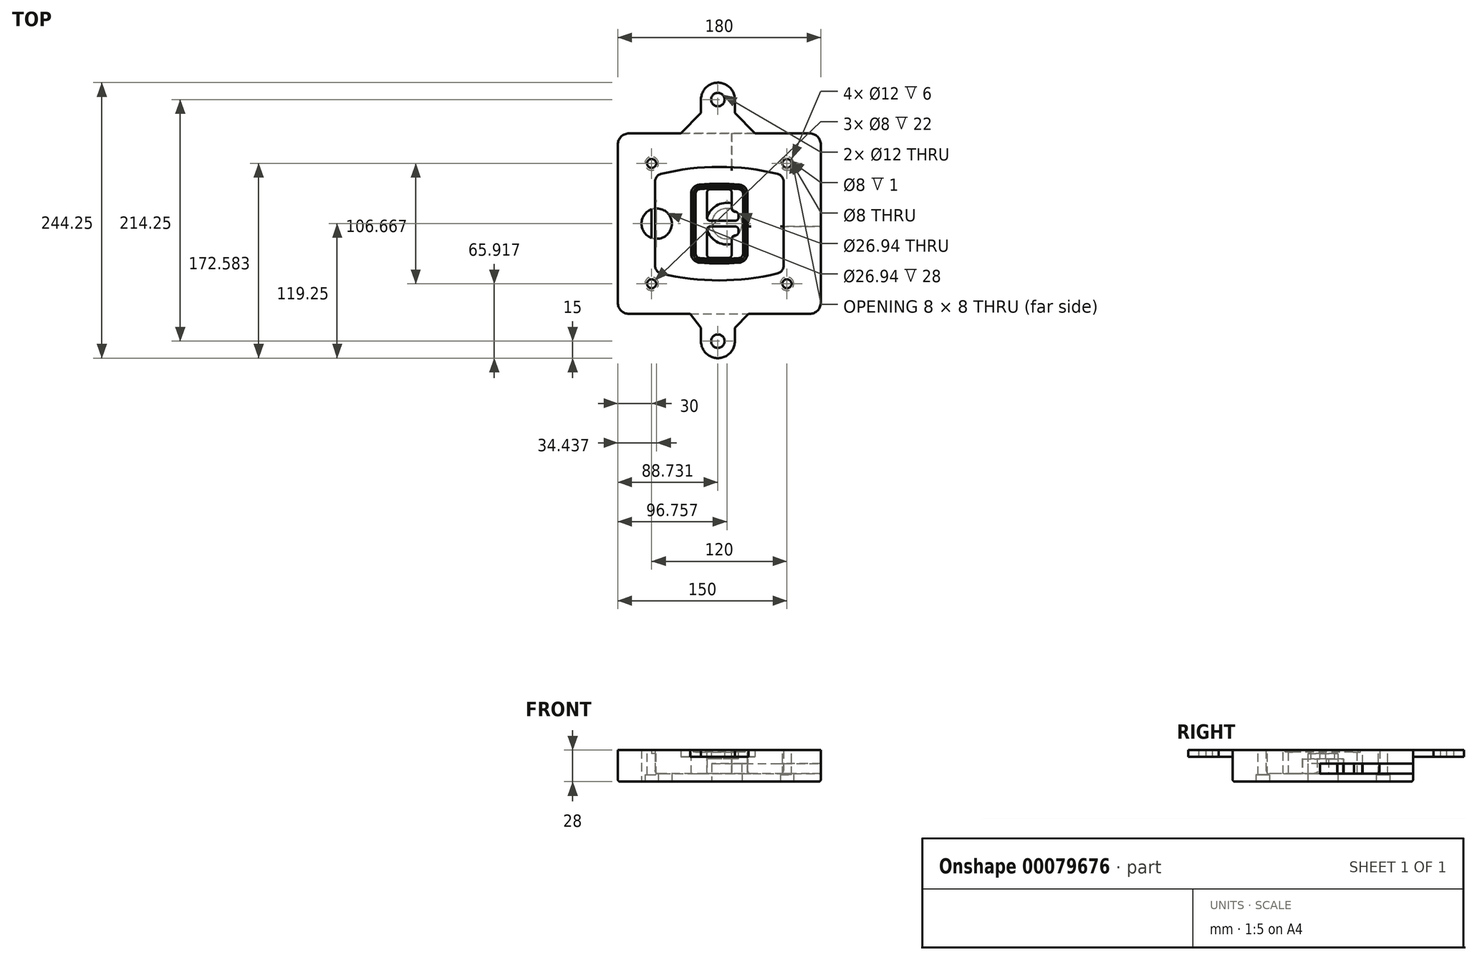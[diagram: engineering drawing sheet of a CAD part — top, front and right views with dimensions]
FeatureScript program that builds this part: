
annotation { "Feature Type Name" : "Feature", "Feature Type Description" : "" }
export const myFeature = defineFeature(function(context is Context, id is Id, definition is map)
    precondition{}
    {
        {
            var Q0;
            Q0=qCreatedBy(makeId("Top.planeOp"),FACE);
            var sketch = newSketch(context, id + "F0", { "sketchPlane" : qUnion([Q0])});
            skPoint(sketch, "E0.rect.middle", {"position": v(0, 0) * mm});
            skLineSegment(sketch, "E1.bottom", {"start": v(-80, -80) * mm, "end": v(80, -80) * mm});
            skLineSegment(sketch, "E1.top", {"start": v(-80, 80) * mm, "end": v(80, 80) * mm});
            skLineSegment(sketch, "E1.left", {"start": v(-90, -70) * mm, "end": v(-90, 70) * mm});
            skLineSegment(sketch, "E1.right", {"start": v(90, -70) * mm, "end": v(90, 70) * mm});
            skLineSegment(sketch, "E2", {"start": v(-90, 80) * mm, "end": v(90, -80) * mm, "construction": true});
            skLineSegment(sketch, "E3", {"start": v(90, 80) * mm, "end": v(-90, -80) * mm, "construction": true});
            skCircle(sketch, "E4", {"center": v(-60, 53.33) * mm, "radius": 4 * mm});
            skCircle(sketch, "E5", {"center": v(60, 53.33) * mm, "radius": 4 * mm});
            skCircle(sketch, "E6", {"center": v(60, -53.33) * mm, "radius": 4 * mm});
            skCircle(sketch, "E7", {"center": v(-60, -53.33) * mm, "radius": 4 * mm});
            skLineSegment(sketch, "E8", {"start": v(-60, 53.33) * mm, "end": v(60, 53.33) * mm, "construction": true});
            skLineSegment(sketch, "E9", {"start": v(60, 53.33) * mm, "end": v(60, -53.33) * mm, "construction": true});
            skLineSegment(sketch, "E10", {"start": v(60, -53.33) * mm, "end": v(-60, -53.33) * mm, "construction": true});
            skLineSegment(sketch, "E11", {"start": v(-60, -53.33) * mm, "end": v(-60, 53.33) * mm, "construction": true});
            skLineSegment(sketch, "E12", {"start": v(-60, 37.3) * mm, "end": v(-60, -37.3) * mm});
            skLineSegment(sketch, "E13", {"start": v(60, 37.3) * mm, "end": v(60, -37.3) * mm});
            skArc(sketch, "E14", {"start": v(52.38, 47.01) * mm, "mid": v(0, 53.33) * mm, "end": v(-52.38, 47.01) * mm});
            skArc(sketch, "E15", {"start": v(-52.38, -47.01) * mm, "mid": v(0, -53.33) * mm, "end": v(52.38, -47.01) * mm});
            skLineSegment(sketch, "E16", {"start": v(-60, 0) * mm, "end": v(60, 0) * mm, "construction": true});
            skPoint(sketch, "E17.visualSharp", {"position": v(-60, -45) * mm});
            skArc(sketch, "E17.filletArc", {"start": v(-60, -37.3) * mm, "mid": v(-57.87, -43.47) * mm, "end": v(-52.38, -47.01) * mm});
            skPoint(sketch, "E18.visualSharp", {"position": v(-60, 45) * mm});
            skArc(sketch, "E18.filletArc", {"start": v(-52.38, 47.01) * mm, "mid": v(-57.87, 43.47) * mm, "end": v(-60, 37.3) * mm});
            skPoint(sketch, "E19.visualSharp", {"position": v(60, 45) * mm});
            skArc(sketch, "E19.filletArc", {"start": v(60, 37.3) * mm, "mid": v(57.87, 43.47) * mm, "end": v(52.38, 47.01) * mm});
            skPoint(sketch, "E20.visualSharp", {"position": v(60, -45) * mm});
            skArc(sketch, "E20.filletArc", {"start": v(52.38, -47.01) * mm, "mid": v(57.87, -43.47) * mm, "end": v(60, -37.3) * mm});
            skPoint(sketch, "E21.visualSharp", {"position": v(-90, 80) * mm});
            skArc(sketch, "E21.filletArc", {"start": v(-80, 80) * mm, "mid": v(-87.07, 77.07) * mm, "end": v(-90, 70) * mm});
            skPoint(sketch, "E22.visualSharp", {"position": v(90, 80) * mm});
            skArc(sketch, "E22.filletArc", {"start": v(90, 70) * mm, "mid": v(87.07, 77.07) * mm, "end": v(80, 80) * mm});
            skPoint(sketch, "E23.visualSharp", {"position": v(90, -80) * mm});
            skArc(sketch, "E23.filletArc", {"start": v(80, -80) * mm, "mid": v(87.07, -77.07) * mm, "end": v(90, -70) * mm});
            skPoint(sketch, "E24.visualSharp", {"position": v(-90, -80) * mm});
            skArc(sketch, "E24.filletArc", {"start": v(-90, -70) * mm, "mid": v(-87.07, -77.07) * mm, "end": v(-80, -80) * mm});
            skArc(sketch, "E25.0", {"start": v(57, 37.3) * mm, "mid": v(55.5, 41.62) * mm, "end": v(51.67, 44.1) * mm});
            skLineSegment(sketch, "E25.1", {"start": v(57, 37.3) * mm, "end": v(57, -37.3) * mm});
            skArc(sketch, "E25.2", {"start": v(51.67, -44.1) * mm, "mid": v(55.5, -41.62) * mm, "end": v(57, -37.3) * mm});
            skArc(sketch, "E25.3", {"start": v(-51.67, -44.1) * mm, "mid": v(0, -50.33) * mm, "end": v(51.67, -44.1) * mm});
            skArc(sketch, "E25.4", {"start": v(-57, -37.3) * mm, "mid": v(-55.5, -41.62) * mm, "end": v(-51.67, -44.1) * mm});
            skArc(sketch, "E25.5", {"start": v(51.67, 44.1) * mm, "mid": v(0, 50.33) * mm, "end": v(-51.67, 44.1) * mm});
            skLineSegment(sketch, "E25.6", {"start": v(-57, 37.3) * mm, "end": v(-57, -37.3) * mm});
            skArc(sketch, "E25.7", {"start": v(-51.67, 44.1) * mm, "mid": v(-55.5, 41.62) * mm, "end": v(-57, 37.3) * mm});
            skArc(sketch, "E26.0", {"start": v(-53.33, 50.9) * mm, "mid": v(-61.01, 45.94) * mm, "end": v(-64, 37.3) * mm});
            skArc(sketch, "E26.1", {"start": v(53.33, 50.9) * mm, "mid": v(0, 57.33) * mm, "end": v(-53.33, 50.9) * mm});
            skArc(sketch, "E26.2", {"start": v(64, 37.3) * mm, "mid": v(61.01, 45.94) * mm, "end": v(53.33, 50.9) * mm});
            skLineSegment(sketch, "E26.3", {"start": v(64, 37.3) * mm, "end": v(64, -37.3) * mm});
            skArc(sketch, "E26.4", {"start": v(53.33, -50.9) * mm, "mid": v(61.01, -45.94) * mm, "end": v(64, -37.3) * mm});
            skLineSegment(sketch, "E26.5", {"start": v(-64, 37.3) * mm, "end": v(-64, -37.3) * mm});
            skArc(sketch, "E26.6", {"start": v(-53.33, -50.9) * mm, "mid": v(0, -57.33) * mm, "end": v(53.33, -50.9) * mm});
            skArc(sketch, "E26.7", {"start": v(-64, -37.3) * mm, "mid": v(-61.01, -45.94) * mm, "end": v(-53.33, -50.9) * mm});
            skSolve(sketch);
        }
        {
            var Q0;
            Q0=makeQuery(id+"F0.imprint","IMPRINT",FACE,{"disambiguationData":[TD([[makeQuery(id+"F0.imprint","IMPRINT",EDGE,{"derivedFrom":sQuery(id+"F0.wireOp",EDGE,"E1.bottom")}),1.0]])]});
            var Q1;
            Q1=makeQuery(id+"F0.imprint","IMPRINT",FACE,{"disambiguationData":[TD([[makeQuery(id+"F0.imprint","IMPRINT",EDGE,{"derivedFrom":sQuery(id+"F0.wireOp",EDGE,"E12")}),1.0]])]});
            var Q2;
            Q2=makeQuery(id+"F0.imprint","IMPRINT",FACE,{"disambiguationData":[TD([[makeQuery(id+"F0.imprint","IMPRINT",EDGE,{"derivedFrom":sQuery(id+"F0.wireOp",EDGE,"E25.0")}),1.0]])]});
            var Q3;
            Q3=makeQuery(id+"F0.imprint","IMPRINT",FACE,{"disambiguationData":[TD([[makeQuery(id+"F0.imprint","IMPRINT",EDGE,{"derivedFrom":sQuery(id+"F0.wireOp",EDGE,"E12")}),-1.0]])]});
            extrude(context, id + "F1", {"entities" : qUnion([Q0, Q1, Q2, Q3]), "oppositeDirection" : true, "depth" : 25 * mm});
        }
        {
            var Q0;
            Q0=makeQuery(id+"F0.imprint","IMPRINT",FACE,{"disambiguationData":[TD([[makeQuery(id+"F0.imprint","IMPRINT",EDGE,{"derivedFrom":sQuery(id+"F0.wireOp",EDGE,"E12")}),1.0]])]});
            extrude(context, id + "F2", {"entities" : qUnion([Q0]), "operationType" : NewBodyOperationType.ADD, "depth" : 3 * mm});
        }
        {
            var Q0;
            Q0=makeQuery(id+"F0.imprint","IMPRINT",FACE,{"disambiguationData":[TD([[makeQuery(id+"F0.imprint","IMPRINT",EDGE,{"derivedFrom":sQuery(id+"F0.wireOp",EDGE,"E25.0")}),1.0]])]});
            extrude(context, id + "F3", {"entities" : qUnion([Q0]), "operationType" : NewBodyOperationType.REMOVE, "oppositeDirection" : true, "depth" : 18 * mm});
        }
        {
            var Q0;
            Q0=makeQuery(id+"F2.opExtrude","CAP_FACE",FACE,{"disambiguationData":[OSD([sQuery(id+"F0.wireOp",EDGE,"E12"),sQuery(id+"F0.wireOp",EDGE,"E13"),sQuery(id+"F0.wireOp",EDGE,"E14"),sQuery(id+"F0.wireOp",EDGE,"E15"),sQuery(id+"F0.wireOp",EDGE,"E17.filletArc"),sQuery(id+"F0.wireOp",EDGE,"E18.filletArc"),sQuery(id+"F0.wireOp",EDGE,"E19.filletArc"),sQuery(id+"F0.wireOp",EDGE,"E20.filletArc"),sQuery(id+"F0.wireOp",EDGE,"E25.0"),sQuery(id+"F0.wireOp",EDGE,"E25.1"),sQuery(id+"F0.wireOp",EDGE,"E25.2"),sQuery(id+"F0.wireOp",EDGE,"E25.3"),sQuery(id+"F0.wireOp",EDGE,"E25.4"),sQuery(id+"F0.wireOp",EDGE,"E25.5"),sQuery(id+"F0.wireOp",EDGE,"E25.6"),sQuery(id+"F0.wireOp",EDGE,"E25.7")])],"isStart":false});
            var sketch = newSketch(context, id + "F4", { "sketchPlane" : qUnion([Q0])});
            skArc(sketch, "E27.0", {"start": v(-17.7, -34.56) * mm, "mid": v(0, -35.33) * mm, "end": v(17.7, -34.56) * mm});
            skArc(sketch, "E28.0", {"start": v(17.7, 34.56) * mm, "mid": v(0, 35.33) * mm, "end": v(-17.7, 34.56) * mm});
            skLineSegment(sketch, "E29", {"start": v(-25, 26.59) * mm, "end": v(-25, -26.59) * mm});
            skLineSegment(sketch, "E30", {"start": v(25, 26.59) * mm, "end": v(25, -26.59) * mm});
            skLineSegment(sketch, "E31", {"start": v(-25, 33.78) * mm, "end": v(25, 33.78) * mm, "construction": true});
            skLineSegment(sketch, "E32", {"start": v(-25, -33.78) * mm, "end": v(25, -33.78) * mm, "construction": true});
            skPoint(sketch, "E33.visualSharp", {"position": v(-25, 33.78) * mm});
            skArc(sketch, "E33.filletArc", {"start": v(-17.7, 34.56) * mm, "mid": v(-22.9, 32) * mm, "end": v(-25, 26.59) * mm});
            skPoint(sketch, "E34.visualSharp", {"position": v(25, 33.78) * mm});
            skArc(sketch, "E34.filletArc", {"start": v(25, 26.59) * mm, "mid": v(22.9, 32) * mm, "end": v(17.7, 34.56) * mm});
            skPoint(sketch, "E35.visualSharp", {"position": v(25, -33.78) * mm});
            skArc(sketch, "E35.filletArc", {"start": v(17.7, -34.56) * mm, "mid": v(22.9, -32) * mm, "end": v(25, -26.59) * mm});
            skPoint(sketch, "E36.visualSharp", {"position": v(-25, -33.78) * mm});
            skArc(sketch, "E36.filletArc", {"start": v(-25, -26.59) * mm, "mid": v(-22.9, -32) * mm, "end": v(-17.7, -34.56) * mm});
            skArc(sketch, "E37.0", {"start": v(51.67, 44.1) * mm, "mid": v(0, 50.33) * mm, "end": v(-51.67, 44.1) * mm});
            skArc(sketch, "E37.1", {"start": v(-51.67, 44.1) * mm, "mid": v(-55.5, 41.62) * mm, "end": v(-57, 37.3) * mm});
            skLineSegment(sketch, "E37.2", {"start": v(-57, 37.3) * mm, "end": v(-57, -37.3) * mm});
            skArc(sketch, "E37.3", {"start": v(-57, -37.3) * mm, "mid": v(-55.5, -41.62) * mm, "end": v(-51.67, -44.1) * mm});
            skArc(sketch, "E37.4", {"start": v(-51.67, -44.1) * mm, "mid": v(0, -50.33) * mm, "end": v(51.67, -44.1) * mm});
            skArc(sketch, "E37.5", {"start": v(51.67, -44.1) * mm, "mid": v(55.5, -41.62) * mm, "end": v(57, -37.3) * mm});
            skLineSegment(sketch, "E37.6", {"start": v(57, 37.3) * mm, "end": v(57, -37.3) * mm});
            skArc(sketch, "E37.7", {"start": v(57, 37.3) * mm, "mid": v(55.5, 41.62) * mm, "end": v(51.67, 44.1) * mm});
            skLineSegment(sketch, "E38.0", {"start": v(23, 26.59) * mm, "end": v(23, -26.59) * mm});
            skArc(sketch, "E38.1", {"start": v(17.53, -32.56) * mm, "mid": v(21.42, -30.64) * mm, "end": v(23, -26.59) * mm});
            skArc(sketch, "E38.2", {"start": v(-17.53, -32.56) * mm, "mid": v(0, -33.33) * mm, "end": v(17.53, -32.56) * mm});
            skArc(sketch, "E38.3", {"start": v(-23, -26.59) * mm, "mid": v(-21.42, -30.64) * mm, "end": v(-17.53, -32.56) * mm});
            skLineSegment(sketch, "E38.4", {"start": v(-23, 26.59) * mm, "end": v(-23, -26.59) * mm});
            skArc(sketch, "E38.5", {"start": v(23, 26.59) * mm, "mid": v(21.42, 30.64) * mm, "end": v(17.53, 32.56) * mm});
            skArc(sketch, "E38.6", {"start": v(-17.53, 32.56) * mm, "mid": v(-21.42, 30.64) * mm, "end": v(-23, 26.59) * mm});
            skArc(sketch, "E38.7", {"start": v(17.53, 32.56) * mm, "mid": v(0, 33.33) * mm, "end": v(-17.53, 32.56) * mm});
            skArc(sketch, "E39.0", {"start": v(21, 26.59) * mm, "mid": v(19.95, 29.29) * mm, "end": v(17.35, 30.57) * mm});
            skLineSegment(sketch, "E39.1", {"start": v(21, 26.59) * mm, "end": v(21, -26.59) * mm});
            skArc(sketch, "E39.2", {"start": v(17.35, -30.57) * mm, "mid": v(19.95, -29.29) * mm, "end": v(21, -26.59) * mm});
            skArc(sketch, "E39.3", {"start": v(-17.35, -30.57) * mm, "mid": v(0, -31.33) * mm, "end": v(17.35, -30.57) * mm});
            skArc(sketch, "E39.4", {"start": v(-21, -26.59) * mm, "mid": v(-19.95, -29.29) * mm, "end": v(-17.35, -30.57) * mm});
            skArc(sketch, "E39.5", {"start": v(17.35, 30.57) * mm, "mid": v(0, 31.33) * mm, "end": v(-17.35, 30.57) * mm});
            skLineSegment(sketch, "E39.6", {"start": v(-21, 26.59) * mm, "end": v(-21, -26.59) * mm});
            skArc(sketch, "E39.7", {"start": v(-17.35, 30.57) * mm, "mid": v(-19.95, 29.29) * mm, "end": v(-21, 26.59) * mm});
            skLineSegment(sketch, "E40", {"start": v(-25, 0) * mm, "end": v(25, 0) * mm, "construction": true});
            skLineSegment(sketch, "E41", {"start": v(-11, 5.5) * mm, "end": v(-11, 27.5) * mm});
            skLineSegment(sketch, "E42", {"start": v(-8, 30.5) * mm, "end": v(8, 30.5) * mm});
            skLineSegment(sketch, "E43", {"start": v(11, 27.5) * mm, "end": v(11, 13.5) * mm});
            skLineSegment(sketch, "E44", {"start": v(14, 10.5) * mm, "end": v(14, 10.5) * mm});
            skLineSegment(sketch, "E45", {"start": v(17, 7.5) * mm, "end": v(17, 5.5) * mm});
            skLineSegment(sketch, "E46", {"start": v(14, 2.5) * mm, "end": v(-8, 2.5) * mm});
            skPoint(sketch, "E47.visualSharp", {"position": v(-11, 30.5) * mm});
            skArc(sketch, "E47.filletArc", {"start": v(-8, 30.5) * mm, "mid": v(-10.12, 29.62) * mm, "end": v(-11, 27.5) * mm});
            skPoint(sketch, "E48.visualSharp", {"position": v(11, 30.5) * mm});
            skArc(sketch, "E48.filletArc", {"start": v(11, 27.5) * mm, "mid": v(10.12, 29.62) * mm, "end": v(8, 30.5) * mm});
            skPoint(sketch, "E49.visualSharp", {"position": v(11, 10.5) * mm});
            skArc(sketch, "E49.filletArc", {"start": v(11, 13.5) * mm, "mid": v(11.88, 11.38) * mm, "end": v(14, 10.5) * mm});
            skPoint(sketch, "E50.visualSharp", {"position": v(17, 10.5) * mm});
            skArc(sketch, "E50.filletArc", {"start": v(17, 7.5) * mm, "mid": v(16.12, 9.62) * mm, "end": v(14, 10.5) * mm});
            skPoint(sketch, "E51.visualSharp", {"position": v(17, 2.5) * mm});
            skArc(sketch, "E51.filletArc", {"start": v(14, 2.5) * mm, "mid": v(16.12, 3.38) * mm, "end": v(17, 5.5) * mm});
            skPoint(sketch, "E52.visualSharp", {"position": v(-11, 2.5) * mm});
            skArc(sketch, "E52.filletArc", {"start": v(-11, 5.5) * mm, "mid": v(-10.12, 3.38) * mm, "end": v(-8, 2.5) * mm});
            skLineSegment(sketch, "E53.0.MirrorCS", {"start": v(14, -2.5) * mm, "end": v(-8, -2.5) * mm});
            skArc(sketch, "E54.0.MirrorCS", {"start": v(-11, -5.5) * mm, "mid": v(-10.12, -3.38) * mm, "end": v(-8, -2.5) * mm});
            skLineSegment(sketch, "E55.0.MirrorCS", {"start": v(-11, -5.5) * mm, "end": v(-11, -27.5) * mm});
            skArc(sketch, "E56.0.MirrorCS", {"start": v(-8, -30.5) * mm, "mid": v(-10.12, -29.62) * mm, "end": v(-11, -27.5) * mm});
            skLineSegment(sketch, "E57.0.MirrorCS", {"start": v(-8, -30.5) * mm, "end": v(8, -30.5) * mm});
            skArc(sketch, "E58.0.MirrorCS", {"start": v(11, -27.5) * mm, "mid": v(10.12, -29.62) * mm, "end": v(8, -30.5) * mm});
            skLineSegment(sketch, "E59.0.MirrorCS", {"start": v(11, -27.5) * mm, "end": v(11, -13.5) * mm});
            skArc(sketch, "E60.0.MirrorCS", {"start": v(11, -13.5) * mm, "mid": v(11.88, -11.38) * mm, "end": v(14, -10.5) * mm});
            skArc(sketch, "E61.0.MirrorCS", {"start": v(17, -7.5) * mm, "mid": v(16.12, -9.62) * mm, "end": v(14, -10.5) * mm});
            skLineSegment(sketch, "E62.0.MirrorCS", {"start": v(17, -7.5) * mm, "end": v(17, -5.5) * mm});
            skArc(sketch, "E63.0.MirrorCS", {"start": v(14, -2.5) * mm, "mid": v(16.12, -3.38) * mm, "end": v(17, -5.5) * mm});
            skSolve(sketch);
        }
        {
            var Q0;
            Q0=makeQuery(id+"F4.imprint","IMPRINT",FACE,{"disambiguationData":[TD([[makeQuery(id+"F4.imprint","IMPRINT",EDGE,{"derivedFrom":sQuery(id+"F4.wireOp",EDGE,"E27.0")}),1.0]])]});
            var Q1;
            Q1=makeQuery(id+"F4.imprint","IMPRINT",FACE,{"disambiguationData":[TD([[makeQuery(id+"F4.imprint","IMPRINT",EDGE,{"derivedFrom":sQuery(id+"F4.wireOp",EDGE,"E38.0")}),-1.0]])]});
            var Q2;
            Q2=makeQuery(id+"F4.imprint","IMPRINT",FACE,{"disambiguationData":[TD([[makeQuery(id+"F4.imprint","IMPRINT",EDGE,{"derivedFrom":sQuery(id+"F4.wireOp",EDGE,"E39.0")}),1.0]])]});
            extrude(context, id + "F5", {"entities" : qUnion([Q0, Q1, Q2]), "operationType" : NewBodyOperationType.ADD, "endBound" : BoundingType.UP_TO_NEXT, "oppositeDirection" : true, "depth" : 25 * mm});
        }
        {
            var Q0;
            Q0=makeQuery(id+"F4.imprint","IMPRINT",FACE,{"disambiguationData":[TD([[makeQuery(id+"F4.imprint","IMPRINT",EDGE,{"derivedFrom":sQuery(id+"F4.wireOp",EDGE,"E38.0")}),-1.0]])]});
            extrude(context, id + "F6", {"entities" : qUnion([Q0]), "operationType" : NewBodyOperationType.REMOVE, "oppositeDirection" : true, "depth" : 2 * mm});
        }
        {
            var Q0;
            Q0=makeQuery(id+"F1.opExtrude","CAP_FACE",FACE,{"disambiguationData":[OSD([sQuery(id+"F0.wireOp",EDGE,"E1.bottom"),sQuery(id+"F0.wireOp",EDGE,"E1.top"),sQuery(id+"F0.wireOp",EDGE,"E1.left"),sQuery(id+"F0.wireOp",EDGE,"E1.right"),sQuery(id+"F0.wireOp",EDGE,"E4"),sQuery(id+"F0.wireOp",EDGE,"E5"),sQuery(id+"F0.wireOp",EDGE,"E6"),sQuery(id+"F0.wireOp",EDGE,"E7"),sQuery(id+"F0.wireOp",EDGE,"E21.filletArc"),sQuery(id+"F0.wireOp",EDGE,"E22.filletArc"),sQuery(id+"F0.wireOp",EDGE,"E23.filletArc"),sQuery(id+"F0.wireOp",EDGE,"E24.filletArc")])],"isStart":false});
            var sketch = newSketch(context, id + "F7", { "sketchPlane" : qUnion([Q0])});
            skCircle(sketch, "E64", {"center": v(6.76, 0) * mm, "radius": 13.47 * mm});
            skCircle(sketch, "E65", {"center": v(-55.56, 0) * mm, "radius": 13.47 * mm});
            skLineSegment(sketch, "E66", {"start": v(90, 0) * mm, "end": v(-90, 0) * mm});
            skCircle(sketch, "E67", {"center": v(6.76, 0) * mm, "radius": 18.47 * mm});
            skCircle(sketch, "E68", {"center": v(60, -53.33) * mm, "radius": 6 * mm});
            skCircle(sketch, "E69", {"center": v(-60, -53.33) * mm, "radius": 6 * mm});
            skCircle(sketch, "E70", {"center": v(-60, 53.33) * mm, "radius": 6 * mm});
            skCircle(sketch, "E71", {"center": v(60, 53.33) * mm, "radius": 6 * mm});
            skSolve(sketch);
        }
        {
            var Q0;
            {var subQ1=sQuery(id+"F7.wireOp",EDGE,"E66");var subQ4=sQuery(id+"F7.wireOp",EDGE,"E64");var subQ6=makeQuery(id+"F7.imprint","INTERSECT",VERTEX,{"disambiguationData":[OD(0.0)],"derivedFrom":[subQ4,subQ1]});Q0=makeQuery(id+"F7.imprint","IMPRINT",FACE,{"disambiguationData":[TD([[makeQuery(id+"F7.imprint","IMPRINT",EDGE,{"disambiguationData":[TD([[subQ6,-1.0]])],"derivedFrom":subQ4}),-1.0]])]});}
            var Q1;
            {var subQ0=sQuery(id+"F7.wireOp",EDGE,"E66");var subQ1=sQuery(id+"F7.wireOp",EDGE,"E64");var subQ3=makeQuery(id+"F7.imprint","INTERSECT",VERTEX,{"disambiguationData":[OD(0.0)],"derivedFrom":[subQ1,subQ0]});Q1=makeQuery(id+"F7.imprint","IMPRINT",FACE,{"disambiguationData":[TD([[makeQuery(id+"F7.imprint","IMPRINT",EDGE,{"disambiguationData":[TD([[subQ3,-1.0]])],"derivedFrom":subQ1}),1.0]])]});}
            var Q2;
            {var subQ0=sQuery(id+"F7.wireOp",EDGE,"E66");var subQ1=sQuery(id+"F7.wireOp",EDGE,"E64");var subQ3=makeQuery(id+"F7.imprint","INTERSECT",VERTEX,{"disambiguationData":[OD(0.0)],"derivedFrom":[subQ1,subQ0]});Q2=makeQuery(id+"F7.imprint","IMPRINT",FACE,{"disambiguationData":[TD([[makeQuery(id+"F7.imprint","IMPRINT",EDGE,{"disambiguationData":[TD([[subQ3,1.0]])],"derivedFrom":subQ1}),1.0]])]});}
            var Q3;
            {var subQ1=sQuery(id+"F7.wireOp",EDGE,"E66");var subQ4=sQuery(id+"F7.wireOp",EDGE,"E64");var subQ6=makeQuery(id+"F7.imprint","INTERSECT",VERTEX,{"disambiguationData":[OD(0.0)],"derivedFrom":[subQ4,subQ1]});Q3=makeQuery(id+"F7.imprint","IMPRINT",FACE,{"disambiguationData":[TD([[makeQuery(id+"F7.imprint","IMPRINT",EDGE,{"disambiguationData":[TD([[subQ6,1.0]])],"derivedFrom":subQ4}),-1.0]])]});}
            extrude(context, id + "F8", {"entities" : qUnion([Q0, Q1, Q2, Q3]), "operationType" : NewBodyOperationType.ADD, "oppositeDirection" : true, "depth" : 20 * mm});
        }
        {
            var Q0;
            {var subQ0=sQuery(id+"F7.wireOp",EDGE,"E66");var subQ1=sQuery(id+"F7.wireOp",EDGE,"E64");var subQ3=makeQuery(id+"F7.imprint","INTERSECT",VERTEX,{"disambiguationData":[OD(0.0)],"derivedFrom":[subQ1,subQ0]});Q0=makeQuery(id+"F7.imprint","IMPRINT",FACE,{"disambiguationData":[TD([[makeQuery(id+"F7.imprint","IMPRINT",EDGE,{"disambiguationData":[TD([[subQ3,-1.0]])],"derivedFrom":subQ1}),1.0]])]});}
            var Q1;
            {var subQ0=sQuery(id+"F7.wireOp",EDGE,"E66");var subQ1=sQuery(id+"F7.wireOp",EDGE,"E64");var subQ3=makeQuery(id+"F7.imprint","INTERSECT",VERTEX,{"disambiguationData":[OD(0.0)],"derivedFrom":[subQ1,subQ0]});Q1=makeQuery(id+"F7.imprint","IMPRINT",FACE,{"disambiguationData":[TD([[makeQuery(id+"F7.imprint","IMPRINT",EDGE,{"disambiguationData":[TD([[subQ3,1.0]])],"derivedFrom":subQ1}),1.0]])]});}
            extrude(context, id + "F9", {"entities" : qUnion([Q0, Q1]), "operationType" : NewBodyOperationType.REMOVE, "oppositeDirection" : true, "depth" : 16 * mm});
        }
        {
            var Q0;
            {var subQ0=sQuery(id+"F7.wireOp",EDGE,"E66");var subQ1=sQuery(id+"F7.wireOp",EDGE,"E65");var subQ3=makeQuery(id+"F7.imprint","INTERSECT",VERTEX,{"disambiguationData":[OD(0.0)],"derivedFrom":[subQ1,subQ0]});Q0=makeQuery(id+"F7.imprint","IMPRINT",FACE,{"disambiguationData":[TD([[makeQuery(id+"F7.imprint","IMPRINT",EDGE,{"disambiguationData":[TD([[subQ3,-1.0]])],"derivedFrom":subQ1}),1.0]])]});}
            var Q1;
            {var subQ0=sQuery(id+"F7.wireOp",EDGE,"E66");var subQ1=sQuery(id+"F7.wireOp",EDGE,"E65");var subQ3=makeQuery(id+"F7.imprint","INTERSECT",VERTEX,{"disambiguationData":[OD(0.0)],"derivedFrom":[subQ1,subQ0]});Q1=makeQuery(id+"F7.imprint","IMPRINT",FACE,{"disambiguationData":[TD([[makeQuery(id+"F7.imprint","IMPRINT",EDGE,{"disambiguationData":[TD([[subQ3,1.0]])],"derivedFrom":subQ1}),1.0]])]});}
            extrude(context, id + "F10", {"entities" : qUnion([Q0, Q1]), "operationType" : NewBodyOperationType.REMOVE, "oppositeDirection" : true, "depth" : 25 * mm});
        }
        {
            var Q0;
            Q0=makeQuery(id+"F7.imprint","IMPRINT",FACE,{"disambiguationData":[TD([[makeQuery(id+"F7.imprint","IMPRINT",EDGE,{"derivedFrom":sQuery(id+"F7.wireOp",EDGE,"E68")}),1.0]])]});
            var Q1;
            Q1=makeQuery(id+"F7.imprint","IMPRINT",FACE,{"disambiguationData":[TD([[makeQuery(id+"F7.imprint","IMPRINT",EDGE,{"derivedFrom":makeQuery(id+"F1.opExtrude","CAP_EDGE",EDGE,{"disambiguationData":[OSD([sQuery(id+"F0.wireOp",EDGE,"E5")])],"isStart":false})}),-1.0]])]});
            var Q2;
            Q2=makeQuery(id+"F7.imprint","IMPRINT",FACE,{"disambiguationData":[TD([[makeQuery(id+"F7.imprint","IMPRINT",EDGE,{"derivedFrom":sQuery(id+"F7.wireOp",EDGE,"E69")}),1.0]])]});
            var Q3;
            Q3=makeQuery(id+"F7.imprint","IMPRINT",FACE,{"disambiguationData":[TD([[makeQuery(id+"F7.imprint","IMPRINT",EDGE,{"derivedFrom":makeQuery(id+"F1.opExtrude","CAP_EDGE",EDGE,{"disambiguationData":[OSD([sQuery(id+"F0.wireOp",EDGE,"E4")])],"isStart":false})}),-1.0]])]});
            var Q4;
            Q4=makeQuery(id+"F7.imprint","IMPRINT",FACE,{"disambiguationData":[TD([[makeQuery(id+"F7.imprint","IMPRINT",EDGE,{"derivedFrom":sQuery(id+"F7.wireOp",EDGE,"E70")}),1.0]])]});
            var Q5;
            Q5=makeQuery(id+"F7.imprint","IMPRINT",FACE,{"disambiguationData":[TD([[makeQuery(id+"F7.imprint","IMPRINT",EDGE,{"derivedFrom":makeQuery(id+"F1.opExtrude","CAP_EDGE",EDGE,{"disambiguationData":[OSD([sQuery(id+"F0.wireOp",EDGE,"E7")])],"isStart":false})}),-1.0]])]});
            var Q6;
            Q6=makeQuery(id+"F7.imprint","IMPRINT",FACE,{"disambiguationData":[TD([[makeQuery(id+"F7.imprint","IMPRINT",EDGE,{"derivedFrom":sQuery(id+"F7.wireOp",EDGE,"E71")}),1.0]])]});
            var Q7;
            Q7=makeQuery(id+"F7.imprint","IMPRINT",FACE,{"disambiguationData":[TD([[makeQuery(id+"F7.imprint","IMPRINT",EDGE,{"derivedFrom":makeQuery(id+"F1.opExtrude","CAP_EDGE",EDGE,{"disambiguationData":[OSD([sQuery(id+"F0.wireOp",EDGE,"E6")])],"isStart":false})}),-1.0]])]});
            extrude(context, id + "F11", {"entities" : qUnion([Q0, Q1, Q2, Q3, Q4, Q5, Q6, Q7]), "operationType" : NewBodyOperationType.REMOVE, "oppositeDirection" : true, "depth" : 6 * mm});
        }
        {
            var Q0;
            Q0=makeQuery(id+"F9.boolean.opBoolean","COPY",FACE,{"derivedFrom":makeQuery(id+"F9.opExtrude","CAP_FACE",FACE,{"disambiguationData":[OSD([sQuery(id+"F7.wireOp",EDGE,"E64")])],"isStart":false})});
            var sketch = newSketch(context, id + "F12", { "sketchPlane" : qUnion([Q0])});
            skArc(sketch, "E72.0", {"start": v(11, -88.19) * mm, "mid": v(97.1, -83.6) * mm, "end": v(92.5, 2.5) * mm});
            skLineSegment(sketch, "E72.1", {"start": v(11, -17.97) * mm, "end": v(11, -17.97) * mm});
            skLineSegment(sketch, "E73", {"start": v(92.5, -105.13) * mm, "end": v(102.3, -105.13) * mm});
            skLineSegment(sketch, "E74.0", {"start": v(92.5, 2.5) * mm, "end": v(14, 2.5) * mm});
            skArc(sketch, "E74.1", {"start": v(14, 2.5) * mm, "mid": v(16.12, 3.38) * mm, "end": v(17, 5.5) * mm});
            skLineSegment(sketch, "E74.2", {"start": v(17, 7.5) * mm, "end": v(17, 5.5) * mm});
            skArc(sketch, "E74.3", {"start": v(17, 7.5) * mm, "mid": v(16.12, 9.62) * mm, "end": v(14, 10.5) * mm});
            skArc(sketch, "E74.4", {"start": v(11, 13.5) * mm, "mid": v(11.88, 11.38) * mm, "end": v(14, 10.5) * mm});
            skLineSegment(sketch, "E74.5", {"start": v(11, 13.5) * mm, "end": v(11, -88.19) * mm});
            skLineSegment(sketch, "E74.7", {"start": v(92.5, -2.5) * mm, "end": v(14, -2.5) * mm});
            skArc(sketch, "E74.8", {"start": v(14, -2.5) * mm, "mid": v(16.12, -3.38) * mm, "end": v(17, -5.5) * mm});
            skLineSegment(sketch, "E74.9", {"start": v(17, -7.5) * mm, "end": v(17, -5.5) * mm});
            skArc(sketch, "E74.10", {"start": v(17, -7.5) * mm, "mid": v(16.12, -9.62) * mm, "end": v(14, -10.5) * mm});
            skArc(sketch, "E74.11", {"start": v(11, -13.5) * mm, "mid": v(11.88, -11.38) * mm, "end": v(14, -10.5) * mm});
            skLineSegment(sketch, "E74.12", {"start": v(11, -17.97) * mm, "end": v(11, -13.5) * mm});
            skPoint(sketch, "E75.orphan", {"position": v(11, -27.5) * mm});
            skPoint(sketch, "E76.orphan", {"position": v(-8, -2.5) * mm});
            skPoint(sketch, "E77.orphan", {"position": v(-8, 2.5) * mm});
            skPoint(sketch, "E78.orphan", {"position": v(11, 27.5) * mm});
            skSolve(sketch);
        }
        {
            var Q0;
            {var subQ7=sQuery(id+"F12.wireOp",EDGE,"E72.0");var subQ14=sQuery(id+"F12.wireOp",EDGE,"E72.1");var subQ16=sQuery(id+"F12.wireOp",EDGE,"E74.1");var subQ18=sQuery(id+"F12.wireOp",EDGE,"E74.8");Q0=qUnion([makeQuery(id+"F12.imprint","IMPRINT",FACE,{"disambiguationData":[TD([[makeQuery(id+"F12.imprint","IMPRINT",EDGE,{"derivedFrom":subQ7}),1.0]])]}),makeQuery(id+"F12.imprint","IMPRINT",FACE,{"disambiguationData":[TD([[makeQuery(id+"F12.imprint","IMPRINT",EDGE,{"derivedFrom":subQ14}),1.0]])]}),makeQuery(id+"F12.imprint","IMPRINT",FACE,{"disambiguationData":[TD([[makeQuery(id+"F12.imprint","IMPRINT",EDGE,{"derivedFrom":subQ16}),1.0]])]}),makeQuery(id+"F12.imprint","IMPRINT",FACE,{"disambiguationData":[TD([[makeQuery(id+"F12.imprint","IMPRINT",EDGE,{"derivedFrom":subQ18}),-1.0]])]})]);}
            var Q1;
            Q1=makeQuery(id+"F5.boolean.opBoolean","SPLIT",FACE,{"disambiguationData":[TD([makeQuery(id+"F5.opExtrude","SWEPT_FACE",FACE,{"disambiguationData":[OSD([sQuery(id+"F4.wireOp",EDGE,"E41")])]})])],"derivedFrom":makeQuery(id+"F3.boolean.opBoolean","COPY",FACE,{"derivedFrom":makeQuery(id+"F3.opExtrude","CAP_FACE",FACE,{"disambiguationData":[OSD([sQuery(id+"F0.wireOp",EDGE,"E25.0"),sQuery(id+"F0.wireOp",EDGE,"E25.1"),sQuery(id+"F0.wireOp",EDGE,"E25.2"),sQuery(id+"F0.wireOp",EDGE,"E25.3"),sQuery(id+"F0.wireOp",EDGE,"E25.4"),sQuery(id+"F0.wireOp",EDGE,"E25.5"),sQuery(id+"F0.wireOp",EDGE,"E25.6"),sQuery(id+"F0.wireOp",EDGE,"E25.7")])],"isStart":false})})});
            extrude(context, id + "F13", {"entities" : qUnion([Q0]), "operationType" : NewBodyOperationType.REMOVE, "endBound" : BoundingType.UP_TO_SURFACE, "endBoundEntityFace" : qUnion([Q1]), "depth" : 25 * mm});
        }
        {
            var Q0;
            Q0=makeQuery(id+"F3.boolean.opBoolean","COPY",EDGE,{"derivedFrom":makeQuery(id+"F3.opExtrude","CAP_EDGE",EDGE,{"disambiguationData":[OSD([sQuery(id+"F0.wireOp",EDGE,"E25.6")])],"isStart":false})});
            var Q1;
            Q1=makeQuery(id+"F8.boolean.opBoolean","INTERSECT",EDGE,{"derivedFrom":[makeQuery(id+"F5.opExtrude","SWEPT_FACE",FACE,{"disambiguationData":[OSD([sQuery(id+"F4.wireOp",EDGE,"E30")])]}),makeQuery(id+"F8.opExtrude","CAP_FACE",FACE,{"disambiguationData":[OSD([sQuery(id+"F7.wireOp",EDGE,"E67")])],"isStart":false})]});
            var Q2;
            Q2=makeQuery(id+"F8.boolean.opBoolean","INTERSECT",EDGE,{"disambiguationData":[OD(1.0)],"derivedFrom":[makeQuery(id+"F5.opExtrude","SWEPT_FACE",FACE,{"disambiguationData":[OSD([sQuery(id+"F4.wireOp",EDGE,"E30")])]}),makeQuery(id+"F8.opExtrude","SWEPT_FACE",FACE,{"disambiguationData":[OSD([sQuery(id+"F7.wireOp",EDGE,"E67")])]})]});
            var Q3;
            {var subQ0=makeQuery(id+"F3.boolean.opBoolean","COPY",FACE,{"derivedFrom":makeQuery(id+"F3.opExtrude","CAP_FACE",FACE,{"disambiguationData":[OSD([sQuery(id+"F0.wireOp",EDGE,"E25.0"),sQuery(id+"F0.wireOp",EDGE,"E25.1"),sQuery(id+"F0.wireOp",EDGE,"E25.2"),sQuery(id+"F0.wireOp",EDGE,"E25.3"),sQuery(id+"F0.wireOp",EDGE,"E25.4"),sQuery(id+"F0.wireOp",EDGE,"E25.5"),sQuery(id+"F0.wireOp",EDGE,"E25.6"),sQuery(id+"F0.wireOp",EDGE,"E25.7")])],"isStart":false})});var subQ1=sQuery(id+"F4.wireOp",EDGE,"E30");Q3=makeQuery(id+"F8.boolean.opBoolean","SPLIT",EDGE,{"disambiguationData":[TD([makeQuery(id+"F5.opExtrude","SWEPT_FACE",FACE,{"disambiguationData":[OSD([sQuery(id+"F4.wireOp",EDGE,"E35.filletArc")])]})])],"derivedFrom":makeQuery(id+"F5.opExtrude","TWEAK_EDGE",EDGE,{"derivedFrom":[subQ0,makeQuery(id+"F4.imprint","IMPRINT",EDGE,{"derivedFrom":subQ1})]})});}
            var Q4;
            {var subQ0=sQuery(id+"F0.wireOp",EDGE,"E25.0");var subQ1=sQuery(id+"F0.wireOp",EDGE,"E25.1");var subQ2=sQuery(id+"F0.wireOp",EDGE,"E25.2");var subQ3=sQuery(id+"F0.wireOp",EDGE,"E25.3");var subQ4=sQuery(id+"F0.wireOp",EDGE,"E25.4");var subQ5=sQuery(id+"F0.wireOp",EDGE,"E25.5");var subQ6=sQuery(id+"F0.wireOp",EDGE,"E25.6");var subQ7=sQuery(id+"F0.wireOp",EDGE,"E25.7");Q4=makeQuery(id+"F8.boolean.opBoolean","INTERSECT",EDGE,{"derivedFrom":[makeQuery(id+"F5.boolean.opBoolean","SPLIT",FACE,{"disambiguationData":[TD([makeQuery(id+"F2.opExtrude","SWEPT_FACE",FACE,{"disambiguationData":[OSD([subQ0])]})])],"derivedFrom":makeQuery(id+"F3.boolean.opBoolean","COPY",FACE,{"derivedFrom":makeQuery(id+"F3.opExtrude","CAP_FACE",FACE,{"disambiguationData":[OSD([subQ0,subQ1,subQ2,subQ3,subQ4,subQ5,subQ6,subQ7])],"isStart":false})})}),makeQuery(id+"F8.opExtrude","SWEPT_FACE",FACE,{"disambiguationData":[OSD([sQuery(id+"F7.wireOp",EDGE,"E67")])]})]});}
            var Q5;
            Q5=makeQuery(id+"F8.boolean.opBoolean","INTERSECT",EDGE,{"disambiguationData":[OD(0.0)],"derivedFrom":[makeQuery(id+"F5.opExtrude","SWEPT_FACE",FACE,{"disambiguationData":[OSD([sQuery(id+"F4.wireOp",EDGE,"E30")])]}),makeQuery(id+"F8.opExtrude","SWEPT_FACE",FACE,{"disambiguationData":[OSD([sQuery(id+"F7.wireOp",EDGE,"E67")])]})]});
            fillet(context, id + "F14", {"entities" : qUnion([Q0, Q1, Q2, Q3, Q4, Q5]), "radius" : 3 * mm, "tangentPropagation" : true, "allowEdgeOverflow" : false});
        }
        {
            var Q0;
            Q0=makeQuery(id+"F1.opExtrude","CAP_EDGE",EDGE,{"disambiguationData":[OSD([sQuery(id+"F0.wireOp",EDGE,"E1.bottom")])],"isStart":false});
            fillet(context, id + "F15", {"entities" : qUnion([Q0]), "radius" : 2 * mm, "tangentPropagation" : true, "allowEdgeOverflow" : false});
        }
        {
            var Q0;
            {var subQ0=sQuery(id+"F0.wireOp",EDGE,"E22.filletArc");var subQ1=sQuery(id+"F0.wireOp",EDGE,"E7");var subQ2=sQuery(id+"F0.wireOp",EDGE,"E6");var subQ3=sQuery(id+"F0.wireOp",EDGE,"E5");var subQ4=sQuery(id+"F0.wireOp",EDGE,"E4");var subQ5=sQuery(id+"F0.wireOp",EDGE,"E1.bottom");var subQ6=sQuery(id+"F0.wireOp",EDGE,"E21.filletArc");var subQ7=sQuery(id+"F0.wireOp",EDGE,"E1.top");var subQ8=sQuery(id+"F0.wireOp",EDGE,"E1.left");var subQ9=sQuery(id+"F0.wireOp",EDGE,"E1.right");var subQ10=sQuery(id+"F0.wireOp",EDGE,"E23.filletArc");var subQ11=sQuery(id+"F0.wireOp",EDGE,"E24.filletArc");Q0=makeQuery(id+"F2.boolean.opBoolean","SPLIT",FACE,{"disambiguationData":[TD([makeQuery(id+"F1.opExtrude","SWEPT_FACE",FACE,{"disambiguationData":[OSD([subQ5])]})])],"derivedFrom":makeQuery(id+"F1.opExtrude","CAP_FACE",FACE,{"disambiguationData":[OSD([subQ5,subQ7,subQ8,subQ9,subQ4,subQ3,subQ2,subQ1,subQ6,subQ0,subQ10,subQ11])],"isStart":true})});}
            var sketch = newSketch(context, id + "F16", { "sketchPlane" : qUnion([Q0])});
            skLineSegment(sketch, "E79", {"start": v(-34.26, 80) * mm, "end": v(-16.26, 98) * mm});
            skLineSegment(sketch, "E80", {"start": v(13.73, 98) * mm, "end": v(31.73, 80) * mm});
            skLineSegment(sketch, "E81", {"start": v(-16.26, 98) * mm, "end": v(-16.26, 109.57) * mm});
            skLineSegment(sketch, "E82", {"start": v(13.73, 98) * mm, "end": v(13.73, 110) * mm});
            skArc(sketch, "E83", {"start": v(13.73, 110) * mm, "mid": v(-1.49, 125) * mm, "end": v(-16.26, 109.57) * mm});
            skCircle(sketch, "E84", {"center": v(-1.27, 110) * mm, "radius": 6 * mm});
            skLineSegment(sketch, "E85", {"start": v(-1.27, 110) * mm, "end": v(-1.27, 80) * mm});
            skLineSegment(sketch, "E86.MirrorCS", {"start": v(-1.27, -104.25) * mm, "end": v(-1.27, -74.25) * mm});
            skLineSegment(sketch, "E87.MirrorCS", {"start": v(-30.25, -74.25) * mm, "end": v(-16.26, -92.25) * mm});
            skLineSegment(sketch, "E88.MirrorCS", {"start": v(13.73, -92.25) * mm, "end": v(31.73, -74.25) * mm});
            skLineSegment(sketch, "E89.MirrorCS", {"start": v(13.73, -92.25) * mm, "end": v(13.73, -104.25) * mm});
            skLineSegment(sketch, "E90.MirrorCS", {"start": v(-16.26, -92.25) * mm, "end": v(-16.26, -103.82) * mm});
            skCircle(sketch, "E91.MirrorC", {"center": v(-1.27, -104.25) * mm, "radius": 6 * mm});
            skArc(sketch, "E92.MirrorCS", {"start": v(13.73, -104.25) * mm, "mid": v(-1.49, -119.25) * mm, "end": v(-16.26, -103.82) * mm});
            skSolve(sketch);
        }
        {
            var Q0;
            {var subQ1=sQuery(id+"F16.wireOp",EDGE,"E79");Q0=makeQuery(id+"F16.imprint","IMPRINT",FACE,{"disambiguationData":[TD([[makeQuery(id+"F16.imprint","IMPRINT",EDGE,{"derivedFrom":subQ1}),-1.0]])]});}
            var Q1;
            Q1=makeQuery(id+"F16.imprint","IMPRINT",FACE,{"disambiguationData":[TD([[makeQuery(id+"F16.imprint","IMPRINT",EDGE,{"derivedFrom":makeQuery(id+"F1.opExtrude","CAP_EDGE",EDGE,{"disambiguationData":[OSD([sQuery(id+"F0.wireOp",EDGE,"E1.left")])],"isStart":true})}),-1.0]])]});
            var Q2;
            {var subQ3=sQuery(id+"F16.wireOp",EDGE,"E87.MirrorCS");Q2=makeQuery(id+"F16.imprint","IMPRINT",FACE,{"disambiguationData":[TD([[makeQuery(id+"F16.imprint","IMPRINT",EDGE,{"derivedFrom":subQ3}),1.0]])]});}
            extrude(context, id + "F17", {"entities" : qUnion([Q0, Q1, Q2]), "operationType" : NewBodyOperationType.ADD, "endBound" : BoundingType.SYMMETRIC, "depth" : 6 * mm});
        }
    });
